# Revit family: HC_Storage Tank_MEPcontent_De Dietrich Thermique_DHW_B
name_source: partatom
category: Mechanical Equipment
revit_build: Autodesk Revit 2018 (Build: 20170223_1515(x64)
units: mm (PartAtom-declared; Revit-internal decimal feet)

## family parameters
Always vertical = Yes
Cut with Voids When Loaded = No
OmniClass Number = 23.75.10.34.11
OmniClass Title = Energy Storage Tanks
Part Type = Normal
Room Calculation Point = No
Round Connector Dimension = Use Diameter
Shared = No
Work Plane-Based = No

## types (3) — shared parameters
Article Description = Large capacity independent DHW calorifiers
Black = Color RGB 020-020-020
Boiler Bottom = 40 mm  [stored 0.131234 ft]
Boiler Top = 40 mm  [stored 0.131234 ft]
Content Supplier URL = www.MEPcontent.com
Custom = No
Description = Large capacity independent DHW calorifiers
Domestic Hot Water Diameter 2 = 19 mm  [stored 0.062336 ft]
Domestic Hot Water Maximum Flow (at ΔT=30K – EN13203-1) = 0.0 L/s
Drain Diameter = 32 mm  [stored 0.104987 ft]
EMCS Version = 2.0
ETIM Article Class = EC010184
Family Version = 11.14
Hydronic Return Diameter = 38 mm
Hydronic Supply Diameter = 38 mm
IFCExportAs = IfcTankType
IFCExportType = NOTDEFINED
MEPcontent Class = STORAGE_TANK_HC
Manufacturer = De Dietrich Thermique
Manufacturer URL = http://www.dedietrich-thermique.fr
Product Line = De Dietrich Thermique
Revit Version = 2018
URL = www.stabiplan.com
Use Nominal Diameter = Yes
White = Color RAL 9016
zero-valued in all types: Offset

## per-type parameters (varying)
| type | A | B | Boiler Body | C | C Outer Diameter | Cap Void 1 | Cap Void 2 | D | Domestic Cold Water Diameter | Domestic Hot Water Diameter 1 | Drain Outer Diameter | E | F | G | GTIN | H | J | K | Manufacturer Art. No. | Radius | Volume |
| B 650 | 1800 mm | 920 mm | 1720 mm | 32 mm  [stored 0.104987 ft] | 42 mm | 464 mm | 468 mm | 1330 mm | 32 mm  [stored 0.104987 ft] | 32 mm  [stored 0.104987 ft] | 34 mm | 1051 mm | 285 mm | 140 mm  [stored 0.459318 ft] | 3661238351516 | 385 mm | 1481 mm | 750 mm | 100011343 | 460 mm | 650.0 L |
| B 800 | 2180 mm | 920 mm | 2100 mm | 32 mm  [stored 0.104987 ft] | 42 mm | 464 mm | 468 mm | 1345 mm | 32 mm  [stored 0.104987 ft] | 32 mm  [stored 0.104987 ft] | 27 mm | 1245 mm | 355 mm | 152 mm | 3661238046825 | 455 mm | 2050 mm | 750 mm | 89759840 | 460 mm | 780.0 L |
| B 1000 | 2170 mm | 1040 mm | 2090 mm | 38 mm | 48 mm | 524 mm | 528 mm | 1355 mm | 38 mm | 38 mm | 27 mm | 1255 mm | 365 mm | 162 mm | 3661238046818 | 465 mm | 1977 mm | 850 mm | 89759841 | 520 mm | 980.0 L |

note: column(s) folded — value = type name in every type: Article Type, Model

note: [stored X ft] marks values corroborated as IEEE doubles in the binary element streams (Revit-internal decimal feet)

## geometry (parser evidence)
native form markers: Sweep x2
no freeform markers — native parametric forms only
